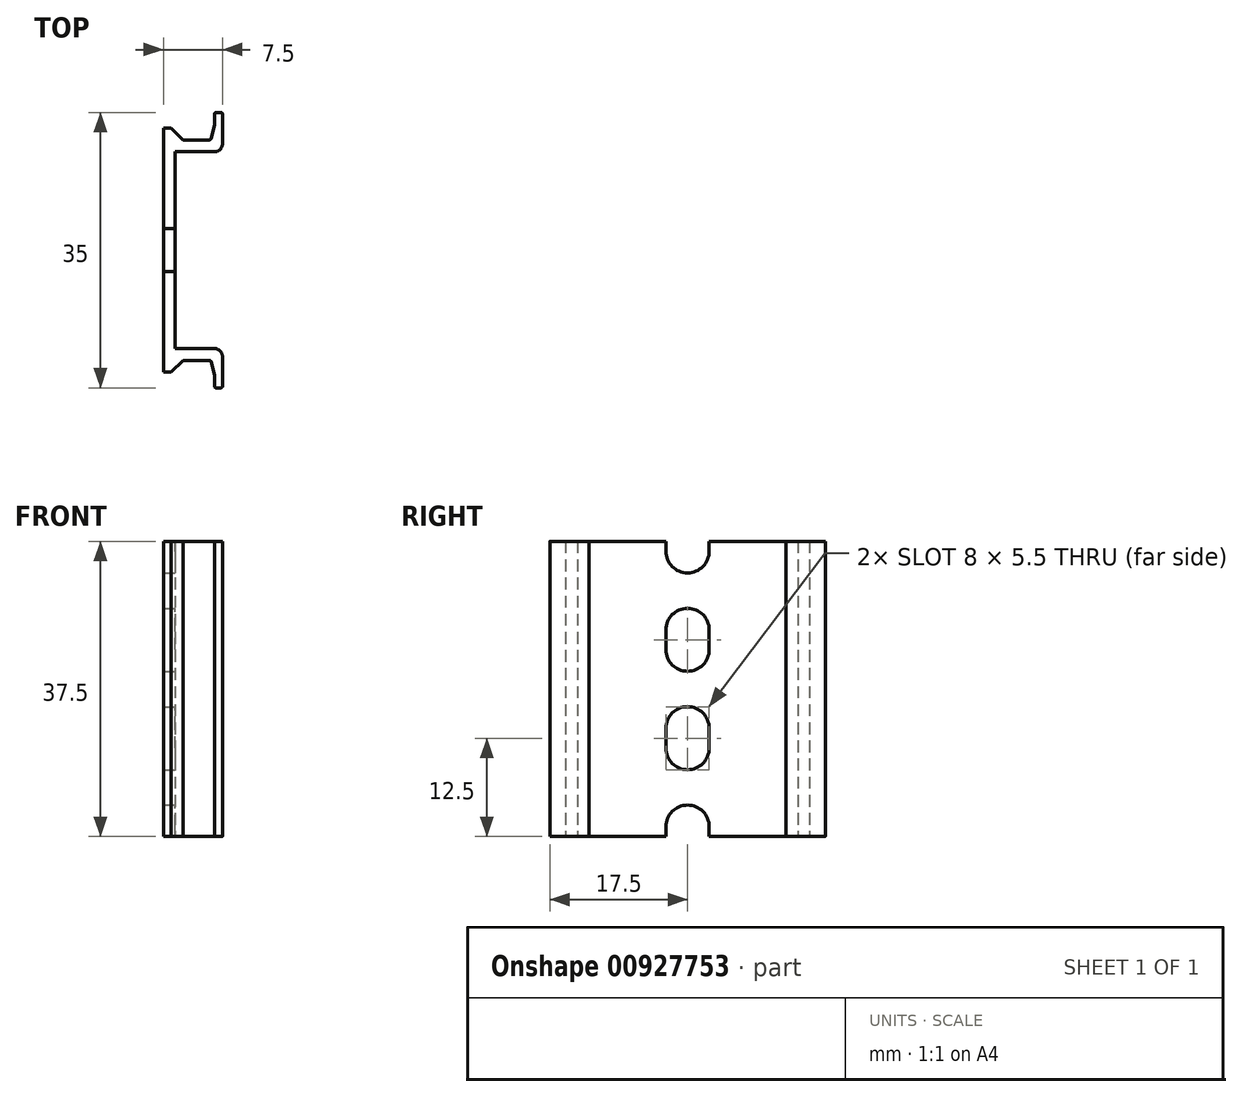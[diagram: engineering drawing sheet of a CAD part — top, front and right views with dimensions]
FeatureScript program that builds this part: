
annotation { "Feature Type Name" : "Feature", "Feature Type Description" : "" }
export const myFeature = defineFeature(function(context is Context, id is Id, definition is map)
    precondition{}
    {
        {
            var Q0;
            Q0=qCreatedBy(makeId("Top.planeOp"),FACE);
            var sketch = newSketch(context, id + "F0", { "sketchPlane" : qUnion([Q0])});
            skLineSegment(sketch, "E0", {"start": v(-87.24, -5.41) * mm, "end": v(-87.24, -17.02) * mm});
            skLineSegment(sketch, "E1", {"start": v(-87.24, -20.22) * mm, "end": v(-87.24, -7.72) * mm});
            skLineSegment(sketch, "E2", {"start": v(-87.24, 4.78) * mm, "end": v(-87.24, -7.72) * mm});
            skLineSegment(sketch, "E3", {"start": v(-79.74, 9.58) * mm, "end": v(-79.74, 5.78) * mm});
            skLineSegment(sketch, "E4", {"start": v(-84.74, 6.28) * mm, "end": v(-81.4, 6.28) * mm});
            skLineSegment(sketch, "E5", {"start": v(-87.24, 7.78) * mm, "end": v(-87.24, -7.72) * mm});
            skLineSegment(sketch, "E6", {"start": v(-85.74, 4.78) * mm, "end": v(-85.74, -7.72) * mm});
            skLineSegment(sketch, "E7", {"start": v(-85.74, 4.78) * mm, "end": v(-80.74, 4.78) * mm});
            skLineSegment(sketch, "E8", {"start": v(-80.54, 9.78) * mm, "end": v(-79.94, 9.78) * mm});
            skLineSegment(sketch, "E9", {"start": v(-80.74, 9.58) * mm, "end": v(-80.74, 8.2) * mm});
            skArc(sketch, "E10", {"start": v(-80.54, 9.78) * mm, "mid": v(-80.68, 9.72) * mm, "end": v(-80.74, 9.58) * mm});
            skArc(sketch, "E11", {"start": v(-79.74, 9.58) * mm, "mid": v(-79.8, 9.72) * mm, "end": v(-79.94, 9.78) * mm});
            skArc(sketch, "E12", {"start": v(-80.74, 4.78) * mm, "mid": v(-80.03, 5.07) * mm, "end": v(-79.74, 5.78) * mm});
            skLineSegment(sketch, "E13", {"start": v(-81.2, 6.43) * mm, "end": v(-80.75, 8.15) * mm});
            skArc(sketch, "E14", {"start": v(-81.4, 6.28) * mm, "mid": v(-81.27, 6.32) * mm, "end": v(-81.2, 6.43) * mm});
            skArc(sketch, "E15", {"start": v(-80.75, 8.15) * mm, "mid": v(-80.74, 8.18) * mm, "end": v(-80.74, 8.2) * mm});
            skLineSegment(sketch, "E16", {"start": v(-87.24, 7.78) * mm, "end": v(-86.24, 7.78) * mm});
            skLineSegment(sketch, "E17", {"start": v(-86.24, 7.78) * mm, "end": v(-84.74, 6.28) * mm});
            skLineSegment(sketch, "E18", {"start": v(-79.74, -25.02) * mm, "end": v(-79.74, -21.22) * mm});
            skLineSegment(sketch, "E19", {"start": v(-84.74, -21.72) * mm, "end": v(-81.4, -21.72) * mm});
            skLineSegment(sketch, "E20", {"start": v(-87.24, -23.22) * mm, "end": v(-87.24, -7.72) * mm});
            skLineSegment(sketch, "E21", {"start": v(-85.74, -20.22) * mm, "end": v(-85.74, -7.72) * mm});
            skLineSegment(sketch, "E22", {"start": v(-85.74, -20.22) * mm, "end": v(-80.74, -20.22) * mm});
            skLineSegment(sketch, "E23", {"start": v(-80.54, -25.22) * mm, "end": v(-79.94, -25.22) * mm});
            skLineSegment(sketch, "E24", {"start": v(-80.74, -25.02) * mm, "end": v(-80.74, -23.65) * mm});
            skArc(sketch, "E25", {"start": v(-80.74, -25.02) * mm, "mid": v(-80.68, -25.16) * mm, "end": v(-80.54, -25.22) * mm});
            skArc(sketch, "E26", {"start": v(-79.94, -25.22) * mm, "mid": v(-79.8, -25.16) * mm, "end": v(-79.74, -25.02) * mm});
            skArc(sketch, "E27", {"start": v(-79.74, -21.22) * mm, "mid": v(-80.03, -20.51) * mm, "end": v(-80.74, -20.22) * mm});
            skLineSegment(sketch, "E28", {"start": v(-81.2, -21.87) * mm, "end": v(-80.75, -23.6) * mm});
            skArc(sketch, "E29", {"start": v(-81.2, -21.87) * mm, "mid": v(-81.27, -21.76) * mm, "end": v(-81.4, -21.72) * mm});
            skArc(sketch, "E30", {"start": v(-80.74, -23.65) * mm, "mid": v(-80.74, -23.62) * mm, "end": v(-80.75, -23.6) * mm});
            skLineSegment(sketch, "E31", {"start": v(-87.24, -23.22) * mm, "end": v(-86.24, -23.22) * mm});
            skLineSegment(sketch, "E32", {"start": v(-86.24, -23.22) * mm, "end": v(-84.74, -21.72) * mm});
            skSolve(sketch);
        }
        {
            var Q0;
            Q0 = qSketchRegion(id + "F0", true);
            extrude(context, id + "F1", {"entities" : qUnion([Q0]), "depth" : 37.5 * mm, "offsetDistance" : 25 * mm});
        }
        {
            var Q0;
            Q0=makeQuery(id+"F1.opExtrude","SWEPT_FACE",FACE,{"disambiguationData":[OSD([sQuery(id+"F0.wireOp",EDGE,"E6"),sQuery(id+"F0.wireOp",EDGE,"E21")])]});
            var sketch = newSketch(context, id + "F2", { "sketchPlane" : qUnion([Q0])});
            skLineSegment(sketch, "E33", {"start": v(-27.44, 25) * mm, "end": v(12.75, 25) * mm, "construction": true});
            skLineSegment(sketch, "E34", {"start": v(-27.61, 12.5) * mm, "end": v(13.17, 12.5) * mm, "construction": true});
            skLineSegment(sketch, "E35", {"start": v(-7.72, 35.65) * mm, "end": v(-7.72, 1.4) * mm, "construction": true});
            skLineSegment(sketch, "E36.left", {"start": v(-4.97, 23.75) * mm, "end": v(-4.97, 26.25) * mm});
            skLineSegment(sketch, "E36.right", {"start": v(-10.47, 23.75) * mm, "end": v(-10.47, 26.25) * mm});
            skPoint(sketch, "E36.middle", {"position": v(-7.72, 25) * mm});
            skArc(sketch, "E37", {"start": v(-4.97, 26.25) * mm, "mid": v(-7.72, 29) * mm, "end": v(-10.47, 26.25) * mm});
            skArc(sketch, "E38", {"start": v(-4.97, 23.75) * mm, "mid": v(-7.72, 21) * mm, "end": v(-10.47, 23.75) * mm});
            skArc(sketch, "E39.0.1.0", {"start": v(-4.97, 13.75) * mm, "mid": v(-7.72, 16.5) * mm, "end": v(-10.47, 13.75) * mm});
            skLineSegment(sketch, "E39.0.1.1", {"start": v(-10.47, 11.25) * mm, "end": v(-10.47, 13.75) * mm});
            skArc(sketch, "E39.0.1.2", {"start": v(-4.97, 11.25) * mm, "mid": v(-7.72, 8.5) * mm, "end": v(-10.47, 11.25) * mm});
            skLineSegment(sketch, "E39.0.1.3", {"start": v(-4.97, 11.25) * mm, "end": v(-4.97, 13.75) * mm});
            skArc(sketch, "E39.0.2.0", {"start": v(-4.97, 1.25) * mm, "mid": v(-7.72, 4) * mm, "end": v(-10.47, 1.25) * mm});
            skLineSegment(sketch, "E39.0.2.1", {"start": v(-10.47, -1.25) * mm, "end": v(-10.47, 1.25) * mm});
            skArc(sketch, "E39.0.2.2", {"start": v(-4.97, -1.25) * mm, "mid": v(-7.72, -4) * mm, "end": v(-10.47, -1.25) * mm});
            skLineSegment(sketch, "E39.0.2.3", {"start": v(-4.97, -1.25) * mm, "end": v(-4.97, 1.25) * mm});
            skLineSegment(sketch, "E39.direction1", {"start": v(-10.47, 23.75) * mm, "end": v(14.53, 23.75) * mm, "construction": true});
            skLineSegment(sketch, "E39.direction2", {"start": v(-10.47, 23.75) * mm, "end": v(-10.47, 11.25) * mm, "construction": true});
            skArc(sketch, "E40.0.1.0", {"start": v(-4.97, 38.75) * mm, "mid": v(-7.72, 41.5) * mm, "end": v(-10.47, 38.75) * mm});
            skLineSegment(sketch, "E40.0.1.1", {"start": v(-10.47, 36.25) * mm, "end": v(-10.47, 38.75) * mm});
            skArc(sketch, "E40.0.1.2", {"start": v(-4.97, 36.25) * mm, "mid": v(-7.72, 33.5) * mm, "end": v(-10.47, 36.25) * mm});
            skLineSegment(sketch, "E40.0.1.3", {"start": v(-4.97, 36.25) * mm, "end": v(-4.97, 38.75) * mm});
            skLineSegment(sketch, "E40.direction2", {"start": v(-10.47, 23.75) * mm, "end": v(-10.47, 36.25) * mm, "construction": true});
            skSolve(sketch);
        }
        {
            var Q0;
            Q0 = qSketchRegion(id + "F2", true);
            extrude(context, id + "F3", {"entities" : qUnion([Q0]), "operationType" : NewBodyOperationType.REMOVE, "oppositeDirection" : true, "depth" : 25 * mm, "offsetDistance" : 25 * mm});
        }
    });
